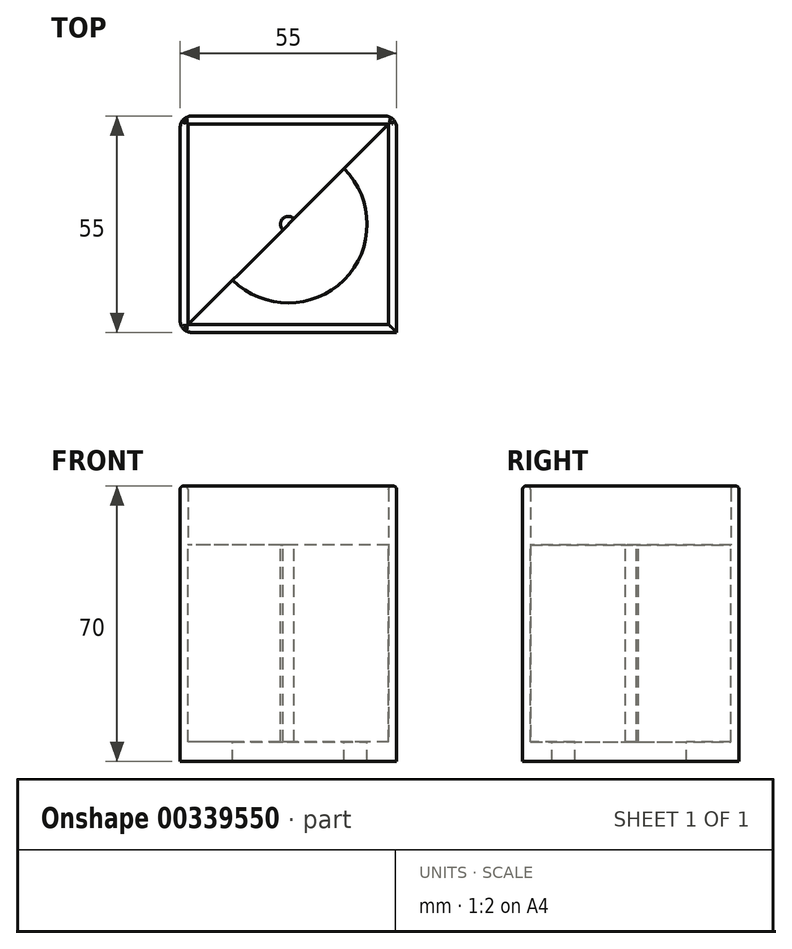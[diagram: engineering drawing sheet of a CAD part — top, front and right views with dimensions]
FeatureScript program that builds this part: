
annotation { "Feature Type Name" : "Feature", "Feature Type Description" : "" }
export const myFeature = defineFeature(function(context is Context, id is Id, definition is map)
    precondition{}
    {
        {
            var Q0;
            Q0=qCreatedBy(makeId("Top.planeOp"),FACE);
            var sketch = newSketch(context, id + "F0", { "sketchPlane" : qUnion([Q0])});
            skLineSegment(sketch, "E0.bottom", {"start": v(0, 0) * mm, "end": v(-51, 0) * mm});
            skLineSegment(sketch, "E0.top", {"start": v(0, 51) * mm, "end": v(-51, 51) * mm});
            skLineSegment(sketch, "E0.left", {"start": v(0, 0) * mm, "end": v(0, 51) * mm});
            skLineSegment(sketch, "E0.right", {"start": v(-51, 0) * mm, "end": v(-51, 51) * mm});
            skLineSegment(sketch, "E1", {"start": v(-51, 0) * mm, "end": v(-51, -2) * mm});
            skLineSegment(sketch, "E2", {"start": v(-51, -2) * mm, "end": v(0, -2) * mm});
            skLineSegment(sketch, "E3", {"start": v(0, 51) * mm, "end": v(2, 51) * mm});
            skLineSegment(sketch, "E4", {"start": v(0, -2) * mm, "end": v(2, -2) * mm});
            skLineSegment(sketch, "E5", {"start": v(2, 51) * mm, "end": v(2, -2) * mm});
            skLineSegment(sketch, "E6.bottom", {"start": v(2, -2) * mm, "end": v(-53, -2) * mm});
            skLineSegment(sketch, "E6.top", {"start": v(2, 53) * mm, "end": v(-53, 53) * mm});
            skLineSegment(sketch, "E6.left", {"start": v(2, -2) * mm, "end": v(2, 53) * mm});
            skLineSegment(sketch, "E6.right", {"start": v(-53, -2) * mm, "end": v(-53, 53) * mm});
            skSolve(sketch);
        }
        {
            var Q0;
            Q0=makeQuery(id+"F0.imprint","IMPRINT",FACE,{"disambiguationData":[TD([[makeQuery(id+"F0.imprint","IMPRINT",EDGE,{"derivedFrom":sQuery(id+"F0.wireOp",EDGE,"E0.bottom")}),-1.0]])]});
            extrude(context, id + "F1", {"entities" : qUnion([Q0]), "depth" : 55 * mm});
        }
        {
            var Q0;
            Q0=makeQuery(id+"F0.imprint","IMPRINT",FACE,{"disambiguationData":[TD([[makeQuery(id+"F0.imprint","IMPRINT",EDGE,{"derivedFrom":sQuery(id+"F0.wireOp",EDGE,"E0.top")}),-1.0]])]});
            var Q1;
            Q1=makeQuery(id+"F0.imprint","IMPRINT",FACE,{"disambiguationData":[TD([[makeQuery(id+"F0.imprint","IMPRINT",EDGE,{"derivedFrom":sQuery(id+"F0.wireOp",EDGE,"E0.bottom")}),1.0]])]});
            extrude(context, id + "F2", {"entities" : qUnion([Q0, Q1]), "operationType" : NewBodyOperationType.ADD, "depth" : 70 * mm});
        }
        {
            var Q0;
            Q0=makeQuery(id+"F1.opExtrude","CAP_FACE",FACE,{"disambiguationData":[OSD([sQuery(id+"F0.wireOp",EDGE,"E0.bottom"),sQuery(id+"F0.wireOp",EDGE,"E0.top"),sQuery(id+"F0.wireOp",EDGE,"E0.left"),sQuery(id+"F0.wireOp",EDGE,"E0.right")])],"isStart":false});
            var sketch = newSketch(context, id + "F3", { "sketchPlane" : qUnion([Q0])});
            skLineSegment(sketch, "E7", {"start": v(-51, 51) * mm, "end": v(0, 0) * mm});
            skLineSegment(sketch, "E8", {"start": v(0, 51) * mm, "end": v(-51, 0) * mm});
            skCircle(sketch, "E9", {"center": v(-25.5, 25.5) * mm, "radius": 20 * mm});
            skCircle(sketch, "E10", {"center": v(-25.5, 25.5) * mm, "radius": 2 * mm});
            skSolve(sketch);
        }
        {
            var Q0;
            {var subQ0=sQuery(id+"F3.wireOp",EDGE,"E9");var subQ1=sQuery(id+"F3.wireOp",EDGE,"E7");var subQ2=makeQuery(id+"F3.imprint","INTERSECT",VERTEX,{"disambiguationData":[OD(0.0)],"derivedFrom":[subQ1,subQ0]});Q0=makeQuery(id+"F3.imprint","IMPRINT",FACE,{"disambiguationData":[TD([[makeQuery(id+"F3.imprint","IMPRINT",EDGE,{"disambiguationData":[TD([[subQ2,-1.0]])],"derivedFrom":subQ1}),-1.0]])]});}
            var Q1;
            {var subQ0=sQuery(id+"F3.wireOp",EDGE,"E8");var subQ1=sQuery(id+"F3.wireOp",EDGE,"E7");var subQ2=makeQuery(id+"F3.imprint","INTERSECT",VERTEX,{"derivedFrom":[subQ1,subQ0]});Q1=makeQuery(id+"F3.imprint","IMPRINT",FACE,{"disambiguationData":[TD([[makeQuery(id+"F3.imprint","IMPRINT",EDGE,{"disambiguationData":[TD([[subQ2,-1.0]])],"derivedFrom":subQ1}),1.0]])]});}
            var Q2;
            {var subQ0=sQuery(id+"F3.wireOp",EDGE,"E8");var subQ1=sQuery(id+"F3.wireOp",EDGE,"E7");var subQ2=makeQuery(id+"F3.imprint","INTERSECT",VERTEX,{"derivedFrom":[subQ1,subQ0]});Q2=makeQuery(id+"F3.imprint","IMPRINT",FACE,{"disambiguationData":[TD([[makeQuery(id+"F3.imprint","IMPRINT",EDGE,{"disambiguationData":[TD([[subQ2,-1.0]])],"derivedFrom":subQ1}),-1.0]])]});}
            var Q3;
            {var subQ0=sQuery(id+"F3.wireOp",EDGE,"E9");var subQ1=sQuery(id+"F3.wireOp",EDGE,"E7");var subQ2=makeQuery(id+"F3.imprint","INTERSECT",VERTEX,{"disambiguationData":[OD(0.0)],"derivedFrom":[subQ1,subQ0]});Q3=makeQuery(id+"F3.imprint","IMPRINT",FACE,{"disambiguationData":[TD([[makeQuery(id+"F3.imprint","IMPRINT",EDGE,{"disambiguationData":[TD([[subQ2,-1.0]])],"derivedFrom":subQ1}),1.0]])]});}
            var Q4;
            {var subQ0=sQuery(id+"F3.wireOp",EDGE,"E10");var subQ1=sQuery(id+"F3.wireOp",EDGE,"E7");var subQ2=makeQuery(id+"F3.imprint","INTERSECT",VERTEX,{"disambiguationData":[OD(0.0)],"derivedFrom":[subQ1,subQ0]});Q4=makeQuery(id+"F3.imprint","IMPRINT",FACE,{"disambiguationData":[TD([[makeQuery(id+"F3.imprint","IMPRINT",EDGE,{"disambiguationData":[TD([[subQ2,-1.0]])],"derivedFrom":subQ1}),-1.0]])]});}
            var Q5;
            {var subQ0=sQuery(id+"F3.wireOp",EDGE,"E10");var subQ1=sQuery(id+"F3.wireOp",EDGE,"E7");var subQ2=makeQuery(id+"F3.imprint","INTERSECT",VERTEX,{"disambiguationData":[OD(1.0)],"derivedFrom":[subQ1,subQ0]});Q5=makeQuery(id+"F3.imprint","IMPRINT",FACE,{"disambiguationData":[TD([[makeQuery(id+"F3.imprint","IMPRINT",EDGE,{"disambiguationData":[TD([[subQ2,-1.0]])],"derivedFrom":subQ1}),1.0]])]});}
            var Q6;
            {var subQ0=sQuery(id+"F3.wireOp",EDGE,"E10");var subQ1=sQuery(id+"F3.wireOp",EDGE,"E7");var subQ2=makeQuery(id+"F3.imprint","INTERSECT",VERTEX,{"disambiguationData":[OD(1.0)],"derivedFrom":[subQ1,subQ0]});Q6=makeQuery(id+"F3.imprint","IMPRINT",FACE,{"disambiguationData":[TD([[makeQuery(id+"F3.imprint","IMPRINT",EDGE,{"disambiguationData":[TD([[subQ2,-1.0]])],"derivedFrom":subQ1}),-1.0]])]});}
            var Q7;
            {var subQ0=sQuery(id+"F3.wireOp",EDGE,"E10");var subQ1=sQuery(id+"F3.wireOp",EDGE,"E7");var subQ2=makeQuery(id+"F3.imprint","INTERSECT",VERTEX,{"disambiguationData":[OD(0.0)],"derivedFrom":[subQ1,subQ0]});Q7=makeQuery(id+"F3.imprint","IMPRINT",FACE,{"disambiguationData":[TD([[makeQuery(id+"F3.imprint","IMPRINT",EDGE,{"disambiguationData":[TD([[subQ2,-1.0]])],"derivedFrom":subQ1}),1.0]])]});}
            extrude(context, id + "F4", {"entities" : qUnion([Q0, Q1, Q2, Q3, Q4, Q5, Q6, Q7]), "operationType" : NewBodyOperationType.REMOVE, "oppositeDirection" : true, "depth" : 50 * mm});
        }
        {
            var Q0;
            {var subQ0=sQuery(id+"F3.wireOp",EDGE,"E10");var subQ1=sQuery(id+"F3.wireOp",EDGE,"E7");var subQ2=makeQuery(id+"F3.imprint","INTERSECT",VERTEX,{"disambiguationData":[OD(0.0)],"derivedFrom":[subQ1,subQ0]});Q0=makeQuery(id+"F3.imprint","IMPRINT",FACE,{"disambiguationData":[TD([[makeQuery(id+"F3.imprint","IMPRINT",EDGE,{"disambiguationData":[TD([[subQ2,-1.0]])],"derivedFrom":subQ1}),1.0]])]});}
            var Q1;
            {var subQ0=sQuery(id+"F3.wireOp",EDGE,"E8");var subQ1=sQuery(id+"F3.wireOp",EDGE,"E7");var subQ2=makeQuery(id+"F3.imprint","INTERSECT",VERTEX,{"derivedFrom":[subQ1,subQ0]});Q1=makeQuery(id+"F3.imprint","IMPRINT",FACE,{"disambiguationData":[TD([[makeQuery(id+"F3.imprint","IMPRINT",EDGE,{"disambiguationData":[TD([[subQ2,-1.0]])],"derivedFrom":subQ1}),1.0]])]});}
            var Q2;
            {var subQ0=sQuery(id+"F3.wireOp",EDGE,"E8");var subQ1=sQuery(id+"F3.wireOp",EDGE,"E7");var subQ2=makeQuery(id+"F3.imprint","INTERSECT",VERTEX,{"derivedFrom":[subQ1,subQ0]});Q2=makeQuery(id+"F3.imprint","IMPRINT",FACE,{"disambiguationData":[TD([[makeQuery(id+"F3.imprint","IMPRINT",EDGE,{"disambiguationData":[TD([[subQ2,-1.0]])],"derivedFrom":subQ1}),-1.0]])]});}
            var Q3;
            {var subQ0=sQuery(id+"F3.wireOp",EDGE,"E10");var subQ1=sQuery(id+"F3.wireOp",EDGE,"E7");var subQ2=makeQuery(id+"F3.imprint","INTERSECT",VERTEX,{"disambiguationData":[OD(0.0)],"derivedFrom":[subQ1,subQ0]});Q3=makeQuery(id+"F3.imprint","IMPRINT",FACE,{"disambiguationData":[TD([[makeQuery(id+"F3.imprint","IMPRINT",EDGE,{"disambiguationData":[TD([[subQ2,-1.0]])],"derivedFrom":subQ1}),-1.0]])]});}
            extrude(context, id + "F5", {"entities" : qUnion([Q0, Q1, Q2, Q3]), "operationType" : NewBodyOperationType.REMOVE, "oppositeDirection" : true, "depth" : 100 * mm});
        }
        {
            var Q0;
            Q0=makeQuery(id+"F2.opExtrude","SWEPT_EDGE",EDGE,{"disambiguationData":[OSD([sQuery(id+"F0.wireOp",EDGE,"E6.top"),sQuery(id+"F0.wireOp",EDGE,"E6.left")])]});
            var Q1;
            Q1=makeQuery(id+"F2.opExtrude","SWEPT_EDGE",EDGE,{"disambiguationData":[OSD([sQuery(id+"F0.wireOp",EDGE,"E6.top"),sQuery(id+"F0.wireOp",EDGE,"E6.right")])]});
            var Q2;
            Q2=makeQuery(id+"F2.opExtrude","SWEPT_EDGE",EDGE,{"disambiguationData":[OSD([sQuery(id+"F0.wireOp",EDGE,"E6.bottom"),sQuery(id+"F0.wireOp",EDGE,"E6.right")])]});
            var Q3;
            Q3=makeQuery(id+"F2.opExtrude","SWEPT_EDGE",EDGE,{"disambiguationData":[OSD([sQuery(id+"F0.wireOp",EDGE,"E6.bottom"),sQuery(id+"F0.wireOp",EDGE,"E6.left")])]});
            fillet(context, id + "F6", {"entities" : qUnion([Q0, Q1, Q2, Q3]), "radius" : 3 * mm, "tangentPropagation" : true, "allowEdgeOverflow" : false});
        }
        {
            var Q0;
            Q0=makeQuery(id+"F2.opExtrude","CAP_EDGE",EDGE,{"disambiguationData":[OSD([sQuery(id+"F0.wireOp",EDGE,"E0.left")])],"isStart":false});
            var Q1;
            Q1=makeQuery(id+"F2.opExtrude","CAP_EDGE",EDGE,{"disambiguationData":[OSD([sQuery(id+"F0.wireOp",EDGE,"E0.top")])],"isStart":false});
            var Q2;
            Q2=makeQuery(id+"F2.opExtrude","CAP_EDGE",EDGE,{"disambiguationData":[OSD([sQuery(id+"F0.wireOp",EDGE,"E0.bottom")])],"isStart":false});
            var Q3;
            Q3=makeQuery(id+"F2.opExtrude","CAP_EDGE",EDGE,{"disambiguationData":[OSD([sQuery(id+"F0.wireOp",EDGE,"E0.right")])],"isStart":false});
            var Q4;
            Q4=makeQuery(id+"F2.opExtrude","CAP_EDGE",EDGE,{"disambiguationData":[OSD([sQuery(id+"F0.wireOp",EDGE,"E6.bottom")])],"isStart":false});
            fillet(context, id + "F7", {"entities" : qUnion([Q0, Q1, Q2, Q3, Q4]), "radius" : 0.9 * mm, "tangentPropagation" : true, "allowEdgeOverflow" : false});
        }
    });
